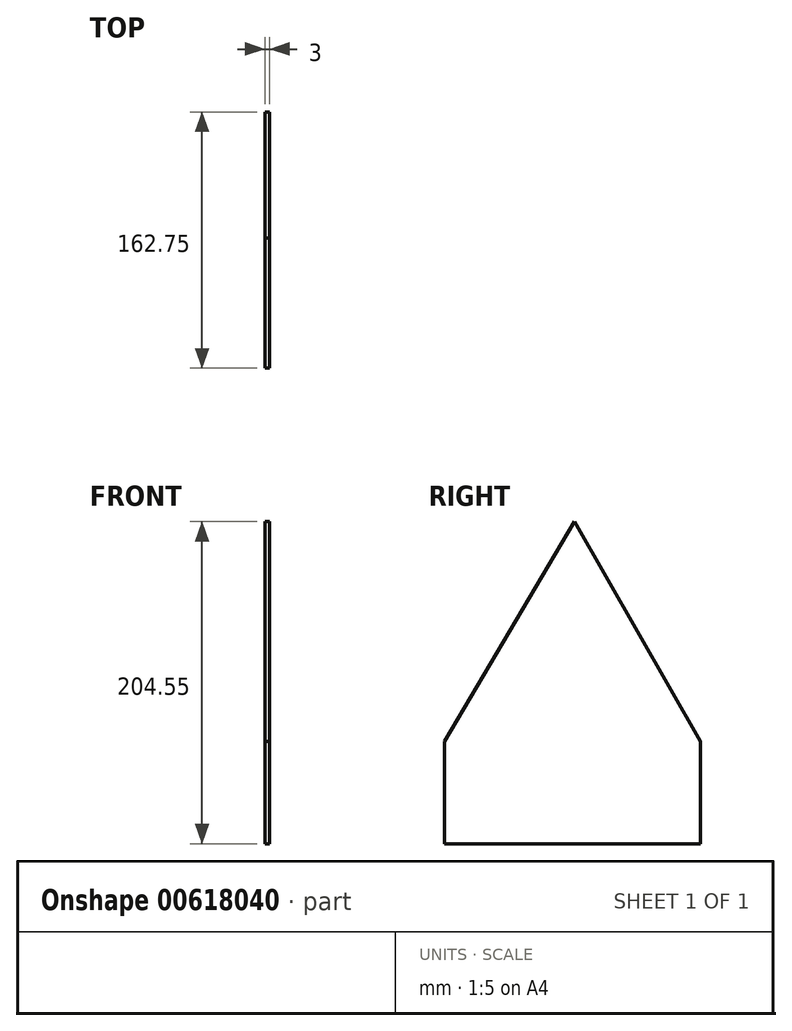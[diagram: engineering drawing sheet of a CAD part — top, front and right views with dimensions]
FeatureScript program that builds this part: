
annotation { "Feature Type Name" : "Feature", "Feature Type Description" : "" }
export const myFeature = defineFeature(function(context is Context, id is Id, definition is map)
    precondition{}
    {
        {
            var Q0;
            Q0=qCreatedBy(makeId("Right.planeOp"),FACE);
            var sketch = newSketch(context, id + "F0", { "sketchPlane" : qUnion([Q0])});
            skLineSegment(sketch, "E0", {"start": v(-82.6, -45.24) * mm, "end": v(80.15, -45.24) * mm});
            skLineSegment(sketch, "E1", {"start": v(80.15, -45.24) * mm, "end": v(0, 94.3) * mm});
            skLineSegment(sketch, "E2", {"start": v(0, 94.3) * mm, "end": v(-82.6, -45.24) * mm});
            skSolve(sketch);
        }
        {
            var Q0;
            Q0=makeQuery(id+"F0.imprint","IMPRINT",FACE,{"disambiguationData":[TD([[makeQuery(id+"F0.imprint","IMPRINT",EDGE,{"derivedFrom":sQuery(id+"F0.wireOp",EDGE,"E0")}),1.0]])]});
            extrude(context, id + "F1", {"entities" : qUnion([Q0]), "depth" : 3 * mm, "offsetDistance" : 25 * mm});
        }
        {
            var Q0;
            Q0=makeQuery(id+"F1.opExtrude","CAP_FACE",FACE,{"disambiguationData":[OSD([sQuery(id+"F0.wireOp",EDGE,"E0"),sQuery(id+"F0.wireOp",EDGE,"E1"),sQuery(id+"F0.wireOp",EDGE,"E2")])],"isStart":true});
            var sketch = newSketch(context, id + "F2", { "sketchPlane" : qUnion([Q0])});
            skLineSegment(sketch, "E3", {"start": v(-80.15, -45.24) * mm, "end": v(-80.15, -110.24) * mm});
            skLineSegment(sketch, "E4", {"start": v(82.6, -45.24) * mm, "end": v(82.6, -110.24) * mm});
            skLineSegment(sketch, "E5", {"start": v(82.6, -110.24) * mm, "end": v(-80.15, -110.24) * mm});
            skSolve(sketch);
        }
        {
            var Q0;
            Q0 = qSketchRegion(id + "F2", true);
            var Q1;
            Q1=makeQuery(id+"F2.imprint","IMPRINT",FACE,{"disambiguationData":[TD([[makeQuery(id+"F2.imprint","IMPRINT",EDGE,{"derivedFrom":sQuery(id+"F2.wireOp",EDGE,"E3")}),1.0]])]});
            extrude(context, id + "F3", {"entities" : qUnion([Q0, Q1]), "operationType" : NewBodyOperationType.ADD, "oppositeDirection" : true, "depth" : 3 * mm, "offsetDistance" : 25 * mm});
        }
    });
